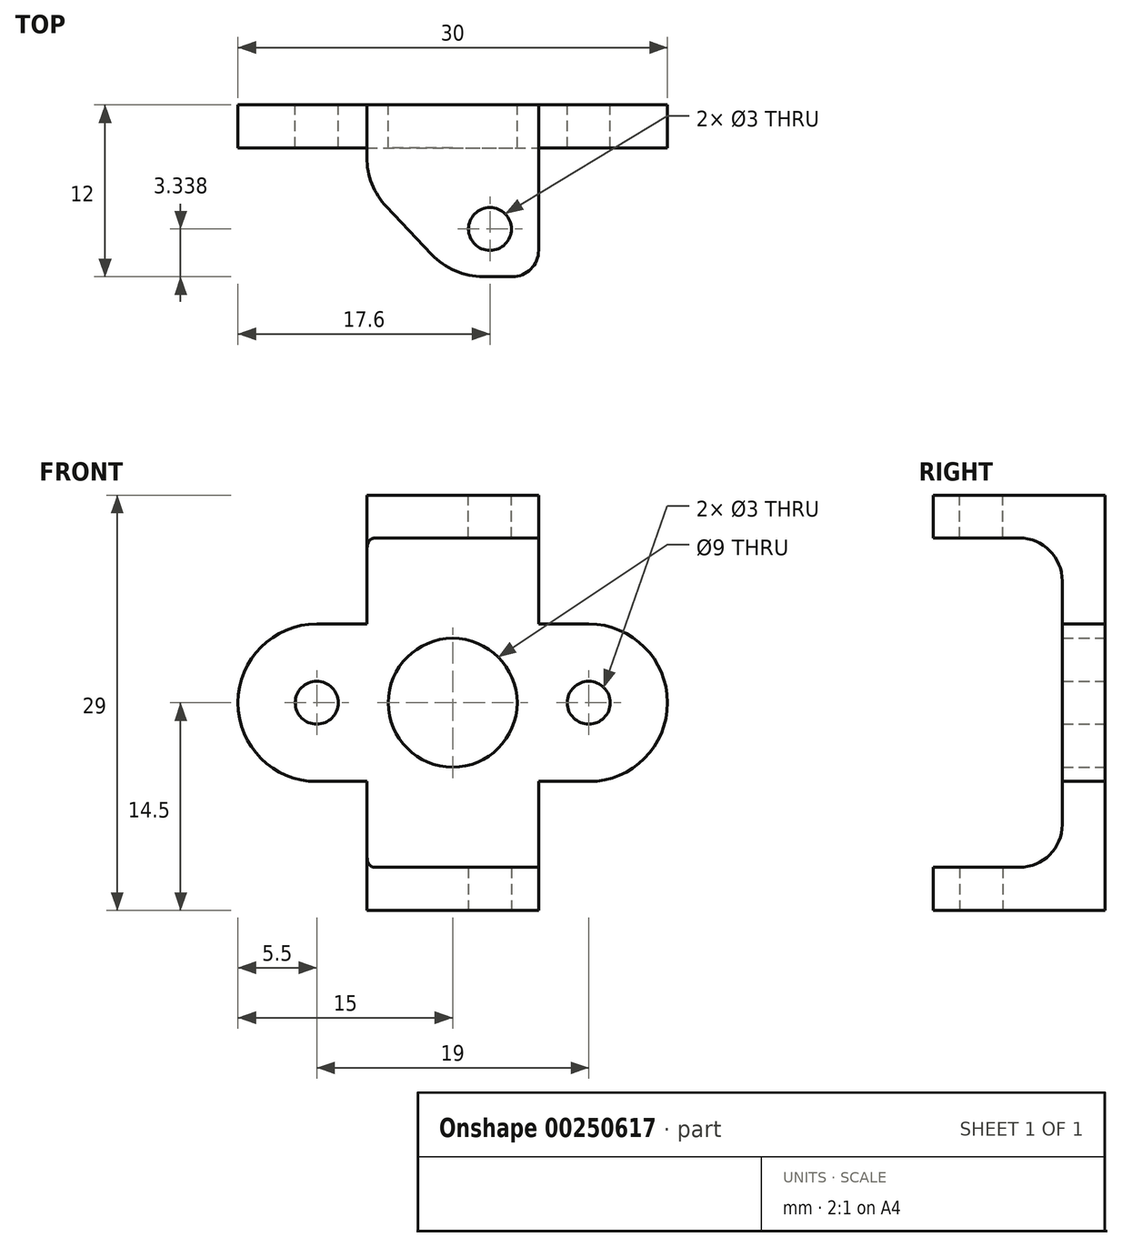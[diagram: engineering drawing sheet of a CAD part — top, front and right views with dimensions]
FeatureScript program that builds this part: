
annotation { "Feature Type Name" : "Feature", "Feature Type Description" : "" }
export const myFeature = defineFeature(function(context is Context, id is Id, definition is map)
    precondition{}
    {
        {
            var Q0;
            Q0=qCreatedBy(makeId("Front.planeOp"),FACE);
            var sketch = newSketch(context, id + "F0", { "sketchPlane" : qUnion([Q0])});
            skCircle(sketch, "E0", {"center": v(0, 0) * mm, "radius": 4.5 * mm});
            skCircle(sketch, "E1", {"center": v(9.5, 0) * mm, "radius": 1.5 * mm});
            skCircle(sketch, "E2.MirrorC", {"center": v(-9.5, 0) * mm, "radius": 1.5 * mm});
            skArc(sketch, "E3.0", {"start": v(9.5, -5.5) * mm, "mid": v(15, 0) * mm, "end": v(9.5, 5.5) * mm});
            skLineSegment(sketch, "E4", {"start": v(9.5, 7.45) * mm, "end": v(9.5, -7.59) * mm, "construction": true});
            skLineSegment(sketch, "E5", {"start": v(9.5, -5.5) * mm, "end": v(0, -5.5) * mm});
            skLineSegment(sketch, "E6.MirrorCS", {"start": v(9.5, 5.5) * mm, "end": v(0, 5.5) * mm});
            skArc(sketch, "E7.MirrorCS", {"start": v(-9.5, -5.5) * mm, "mid": v(-15, 0) * mm, "end": v(-9.5, 5.5) * mm});
            skLineSegment(sketch, "E8.MirrorCS", {"start": v(-9.5, 5.5) * mm, "end": v(0, 5.5) * mm});
            skLineSegment(sketch, "E9.MirrorCS", {"start": v(-9.5, -5.5) * mm, "end": v(0, -5.5) * mm});
            skSolve(sketch);
        }
        {
            var Q0;
            Q0=qSketchRegion(id+"F0",true);
            extrude(context, id + "F1", {"entities" : qUnion([Q0]), "depth" : 3 * mm});
        }
        {
            var Q0;
            Q0=makeQuery(id+"F1.opExtrude","CAP_FACE",FACE,{"disambiguationData":[OSD([sQuery(id+"F0.wireOp",EDGE,"E0"),sQuery(id+"F0.wireOp",EDGE,"E1"),sQuery(id+"F0.wireOp",EDGE,"E2.MirrorC"),sQuery(id+"F0.wireOp",EDGE,"E3.0"),sQuery(id+"F0.wireOp",EDGE,"E5"),sQuery(id+"F0.wireOp",EDGE,"E6.MirrorCS"),sQuery(id+"F0.wireOp",EDGE,"E7.MirrorCS"),sQuery(id+"F0.wireOp",EDGE,"E8.MirrorCS"),sQuery(id+"F0.wireOp",EDGE,"E9.MirrorCS")])],"isStart":false});
            var sketch = newSketch(context, id + "F2", { "sketchPlane" : qUnion([Q0])});
            skLineSegment(sketch, "E10.rect.bottom", {"start": v(6, -14.5) * mm, "end": v(-6, -14.5) * mm});
            skLineSegment(sketch, "E10.rect.top", {"start": v(6, 14.5) * mm, "end": v(-6, 14.5) * mm});
            skLineSegment(sketch, "E10.rect.left", {"start": v(6, -14.5) * mm, "end": v(6, 14.5) * mm});
            skLineSegment(sketch, "E10.rect.right", {"start": v(-6, -14.5) * mm, "end": v(-6, 14.5) * mm});
            skPoint(sketch, "E10.rect.middle", {"position": v(0, 0) * mm});
            skSolve(sketch);
        }
        {
            var Q0;
            Q0=qSketchRegion(id+"F2",true);
            extrude(context, id + "F3", {"entities" : qUnion([Q0]), "operationType" : NewBodyOperationType.ADD, "oppositeDirection" : true, "depth" : 3 * mm});
        }
        {
            var Q0;
            Q0=makeQuery(id+"F3.opExtrude","SWEPT_FACE",FACE,{"disambiguationData":[OSD([sQuery(id+"F2.wireOp",EDGE,"E10.rect.bottom")])]});
            var sketch = newSketch(context, id + "F4", { "sketchPlane" : qUnion([Q0])});
            skLineSegment(sketch, "E11.bottom", {"start": v(6, 0) * mm, "end": v(-6, 0) * mm});
            skLineSegment(sketch, "E11.top", {"start": v(4.15, 12) * mm, "end": v(2.15, 12) * mm});
            skLineSegment(sketch, "E11.left", {"start": v(6, 0) * mm, "end": v(6, 10.15) * mm});
            skLineSegment(sketch, "E11.right", {"start": v(-6, 0) * mm, "end": v(-6, 3.67) * mm});
            skPoint(sketch, "E12.visualSharp", {"position": v(6, 12) * mm});
            skArc(sketch, "E12.filletArc", {"start": v(6, 10.15) * mm, "mid": v(5.46, 11.46) * mm, "end": v(4.15, 12) * mm});
            skCircle(sketch, "E13", {"center": v(2.6, 8.66) * mm, "radius": 1.5 * mm});
            skLineSegment(sketch, "E14", {"start": v(-1.48, 10.44) * mm, "end": v(-4.63, 7.11) * mm});
            skPoint(sketch, "E15.orphan", {"position": v(-6, 12) * mm});
            skPoint(sketch, "E16.visualSharp", {"position": v(-6, 5.67) * mm});
            skArc(sketch, "E16.filletArc", {"start": v(-4.63, 7.11) * mm, "mid": v(-5.64, 5.53) * mm, "end": v(-6, 3.67) * mm});
            skPoint(sketch, "E17.visualSharp", {"position": v(0, 12) * mm});
            skArc(sketch, "E17.filletArc", {"start": v(2.15, 12) * mm, "mid": v(0.17, 11.6) * mm, "end": v(-1.48, 10.44) * mm});
            skSolve(sketch);
        }
        {
            var Q0;
            Q0=qSketchRegion(id+"F4",true);
            extrude(context, id + "F5", {"entities" : qUnion([Q0]), "oppositeDirection" : true, "depth" : 3 * mm});
        }
        {
            var Q0;
            Q0=makeQuery(id+"F5.opExtrude","SWEPT_BODY",BODY,{"disambiguationData":[OSD([sQuery(id+"F4.wireOp",EDGE,"E11.bottom"),sQuery(id+"F4.wireOp",EDGE,"E11.top"),sQuery(id+"F4.wireOp",EDGE,"E11.left"),sQuery(id+"F4.wireOp",EDGE,"E11.right"),sQuery(id+"F4.wireOp",EDGE,"E12.filletArc"),sQuery(id+"F4.wireOp",EDGE,"E13"),sQuery(id+"F4.wireOp",EDGE,"E14"),sQuery(id+"F4.wireOp",EDGE,"E16.filletArc"),sQuery(id+"F4.wireOp",EDGE,"E17.filletArc")])]});
            var Q1;
            Q1=qCreatedBy(makeId("Top.planeOp"),FACE);
            mirror(context, id + "F6", {"operationType" : NewBodyOperationType.ADD, "entities" : qUnion([Q0]), "mirrorPlane" : qUnion([Q1])});
        }
        {
            var Q0;
            Q0=makeQuery(id+"F6.boolean.opBoolean","INTERSECT",EDGE,{"derivedFrom":[makeQuery(id+"F3.boolean.opBoolean","MERGE",FACE,{"derivedFrom":[makeQuery(id+"F1.opExtrude","CAP_FACE",FACE,{"disambiguationData":[OSD([sQuery(id+"F0.wireOp",EDGE,"E0"),sQuery(id+"F0.wireOp",EDGE,"E1"),sQuery(id+"F0.wireOp",EDGE,"E2.MirrorC"),sQuery(id+"F0.wireOp",EDGE,"E3.0"),sQuery(id+"F0.wireOp",EDGE,"E5"),sQuery(id+"F0.wireOp",EDGE,"E6.MirrorCS"),sQuery(id+"F0.wireOp",EDGE,"E7.MirrorCS"),sQuery(id+"F0.wireOp",EDGE,"E8.MirrorCS"),sQuery(id+"F0.wireOp",EDGE,"E9.MirrorCS")])],"isStart":false}),makeQuery(id+"F3.opExtrude","CAP_FACE",FACE,{"disambiguationData":[OSD([sQuery(id+"F2.wireOp",EDGE,"E10.rect.bottom"),sQuery(id+"F2.wireOp",EDGE,"E10.rect.top"),sQuery(id+"F2.wireOp",EDGE,"E10.rect.left"),sQuery(id+"F2.wireOp",EDGE,"E10.rect.right")])],"isStart":true})]}),makeQuery(id+"F6.opPattern","COPY",FACE,{"derivedFrom":makeQuery(id+"F5.opExtrude","CAP_FACE",FACE,{"disambiguationData":[OSD([sQuery(id+"F4.wireOp",EDGE,"E11.bottom"),sQuery(id+"F4.wireOp",EDGE,"E11.top"),sQuery(id+"F4.wireOp",EDGE,"E11.left"),sQuery(id+"F4.wireOp",EDGE,"E11.right"),sQuery(id+"F4.wireOp",EDGE,"E12.filletArc"),sQuery(id+"F4.wireOp",EDGE,"E13"),sQuery(id+"F4.wireOp",EDGE,"E14"),sQuery(id+"F4.wireOp",EDGE,"E16.filletArc"),sQuery(id+"F4.wireOp",EDGE,"E17.filletArc")])],"isStart":false}),"instanceName":"1"})]});
            var Q1;
            Q1=makeQuery(id+"F6.boolean.opBoolean","INTERSECT",EDGE,{"derivedFrom":[makeQuery(id+"F3.boolean.opBoolean","MERGE",FACE,{"derivedFrom":[makeQuery(id+"F1.opExtrude","CAP_FACE",FACE,{"disambiguationData":[OSD([sQuery(id+"F0.wireOp",EDGE,"E0"),sQuery(id+"F0.wireOp",EDGE,"E1"),sQuery(id+"F0.wireOp",EDGE,"E2.MirrorC"),sQuery(id+"F0.wireOp",EDGE,"E3.0"),sQuery(id+"F0.wireOp",EDGE,"E5"),sQuery(id+"F0.wireOp",EDGE,"E6.MirrorCS"),sQuery(id+"F0.wireOp",EDGE,"E7.MirrorCS"),sQuery(id+"F0.wireOp",EDGE,"E8.MirrorCS"),sQuery(id+"F0.wireOp",EDGE,"E9.MirrorCS")])],"isStart":false}),makeQuery(id+"F3.opExtrude","CAP_FACE",FACE,{"disambiguationData":[OSD([sQuery(id+"F2.wireOp",EDGE,"E10.rect.bottom"),sQuery(id+"F2.wireOp",EDGE,"E10.rect.top"),sQuery(id+"F2.wireOp",EDGE,"E10.rect.left"),sQuery(id+"F2.wireOp",EDGE,"E10.rect.right")])],"isStart":true})]}),makeQuery(id+"F5.opExtrude","CAP_FACE",FACE,{"disambiguationData":[OSD([sQuery(id+"F4.wireOp",EDGE,"E11.bottom"),sQuery(id+"F4.wireOp",EDGE,"E11.top"),sQuery(id+"F4.wireOp",EDGE,"E11.left"),sQuery(id+"F4.wireOp",EDGE,"E11.right"),sQuery(id+"F4.wireOp",EDGE,"E12.filletArc"),sQuery(id+"F4.wireOp",EDGE,"E13"),sQuery(id+"F4.wireOp",EDGE,"E14"),sQuery(id+"F4.wireOp",EDGE,"E16.filletArc"),sQuery(id+"F4.wireOp",EDGE,"E17.filletArc")])],"isStart":false})]});
            fillet(context, id + "F7", {"entities" : qUnion([Q0, Q1]), "radius" : 3 * mm, "tangentPropagation" : true, "allowEdgeOverflow" : false});
        }
        {
            var Q0;
            Q0=makeQuery(id+"F3.boolean.opBoolean","MERGE",FACE,{"derivedFrom":[makeQuery(id+"F1.opExtrude","CAP_FACE",FACE,{"disambiguationData":[OSD([sQuery(id+"F0.wireOp",EDGE,"E0"),sQuery(id+"F0.wireOp",EDGE,"E1"),sQuery(id+"F0.wireOp",EDGE,"E2.MirrorC"),sQuery(id+"F0.wireOp",EDGE,"E3.0"),sQuery(id+"F0.wireOp",EDGE,"E5"),sQuery(id+"F0.wireOp",EDGE,"E6.MirrorCS"),sQuery(id+"F0.wireOp",EDGE,"E7.MirrorCS"),sQuery(id+"F0.wireOp",EDGE,"E8.MirrorCS"),sQuery(id+"F0.wireOp",EDGE,"E9.MirrorCS")])],"isStart":true}),makeQuery(id+"F3.opExtrude","CAP_FACE",FACE,{"disambiguationData":[OSD([sQuery(id+"F2.wireOp",EDGE,"E10.rect.bottom"),sQuery(id+"F2.wireOp",EDGE,"E10.rect.top"),sQuery(id+"F2.wireOp",EDGE,"E10.rect.left"),sQuery(id+"F2.wireOp",EDGE,"E10.rect.right")])],"isStart":false})]});
            var sketch = newSketch(context, id + "F8", { "sketchPlane" : qUnion([Q0])});
            skCircle(sketch, "E18", {"center": v(0, 0) * mm, "radius": 4.5 * mm});
            skSolve(sketch);
        }
        {
            var Q0;
            Q0=qSketchRegion(id+"F8",true);
            extrude(context, id + "F9", {"entities" : qUnion([Q0]), "operationType" : NewBodyOperationType.REMOVE, "endBound" : BoundingType.UP_TO_NEXT, "oppositeDirection" : true, "depth" : 25 * mm});
        }
    });
